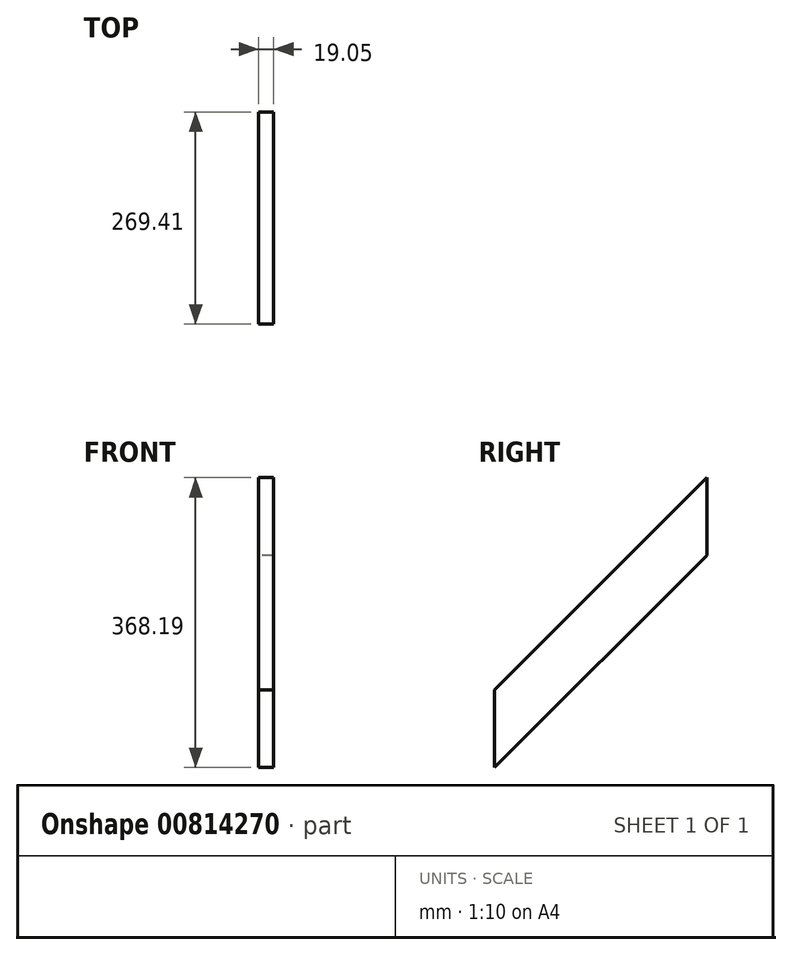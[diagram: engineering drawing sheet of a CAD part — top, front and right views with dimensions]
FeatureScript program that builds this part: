
annotation { "Feature Type Name" : "Feature", "Feature Type Description" : "" }
export const myFeature = defineFeature(function(context is Context, id is Id, definition is map)
    precondition{}
    {
        {
            var Q0;
            Q0=qCreatedBy(makeId("Right.planeOp"),FACE);
            var sketch = newSketch(context, id + "F0", { "sketchPlane" : qUnion([Q0])});
            skLineSegment(sketch, "E0", {"start": v(-269.4, 0) * mm, "end": v(0, 269.4) * mm});
            skLineSegment(sketch, "E1", {"start": v(-269.4, 0) * mm, "end": v(-269.4, 98.78) * mm});
            skLineSegment(sketch, "E2", {"start": v(-269.4, 98.78) * mm, "end": v(0, 368.2) * mm});
            skLineSegment(sketch, "E3", {"start": v(0, 368.2) * mm, "end": v(0, 269.4) * mm});
            skSolve(sketch);
        }
        {
            var Q0;
            Q0 = qSketchRegion(id + "F0", true);
            extrude(context, id + "F1", {"entities" : qUnion([Q0]), "depth" : 19.05 * mm, "offsetDistance" : 25.4 * mm});
        }
    });
